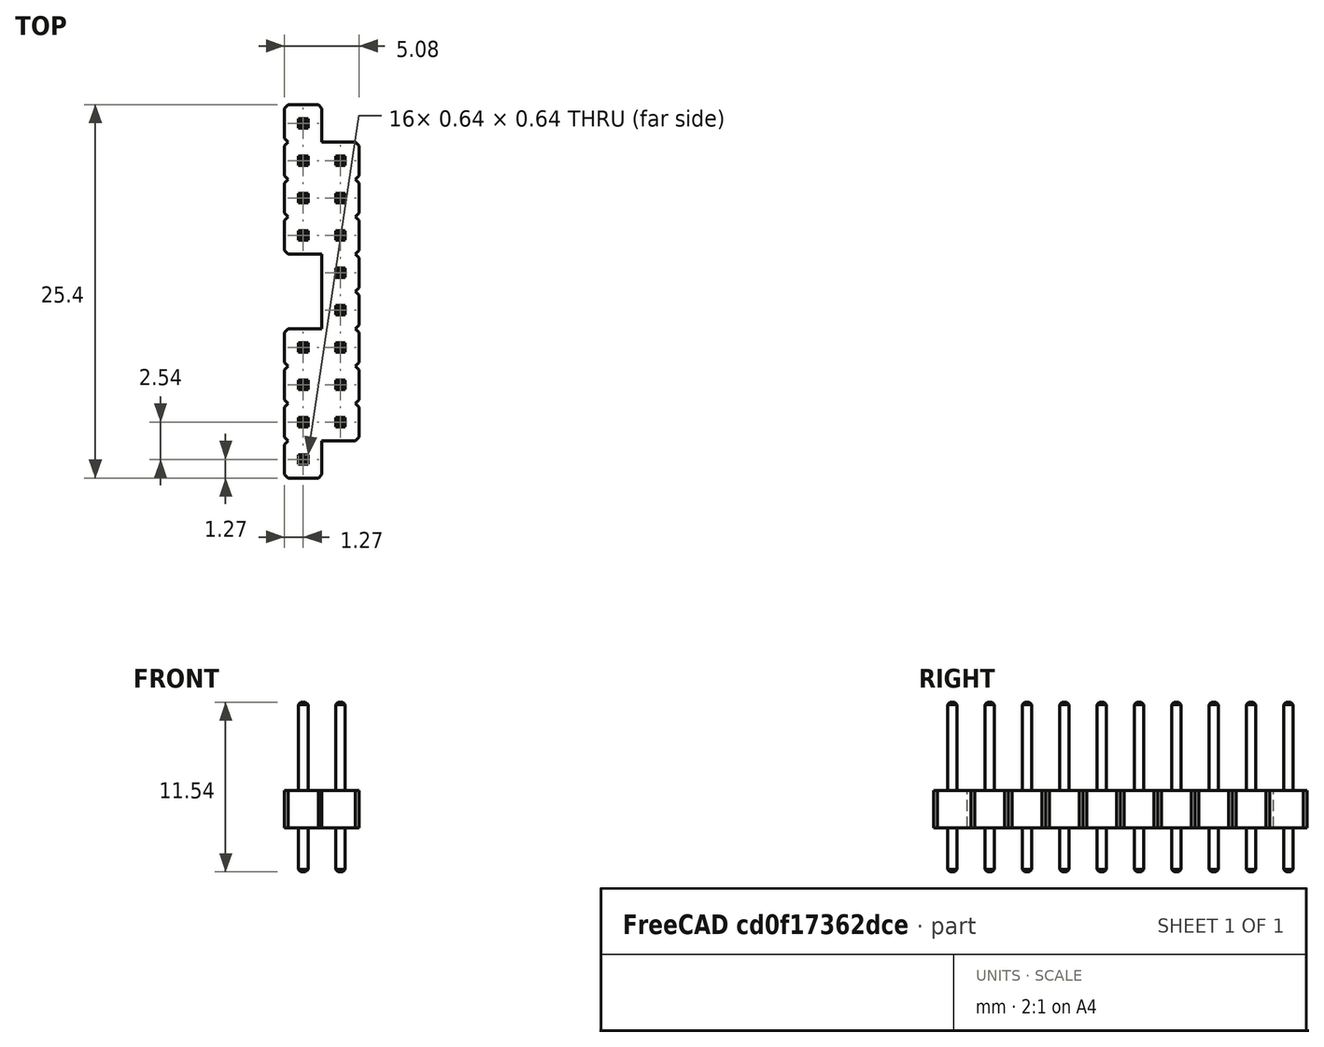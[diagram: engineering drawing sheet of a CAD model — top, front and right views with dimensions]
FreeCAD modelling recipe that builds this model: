
FCSTD DOCUMENT  (FreeCAD 0.18R16146 (Git))
Label: ce-header
License: All rights reserved
LicenseURL: http://en.wikipedia.org/wiki/All_rights_reserved
objects: Part::Box×3, Part::Cut×3, Part::Feature×1, Part::Chamfer×1
note: 8 computed .brp shape members not serialized (recipe doc carries the construction recipe); baked Part::Feature solids carry a one-line shape summary decoded from their .brp

FEATURE [Part::Feature] Part__Feature  label="PinHeader_2x10_P254mm_Vertical"
  shape: bbox 5.08 x 25.4 x 11.54 mm, 424 faces (baked)
FEATURE [Part::Box] Box  label="Cube"
  AttacherType = Attacher::AttachEngine3D
  Height = 20
  Length = 2.54
  Placement = pos=(1.27,-1.27,-8) rot=(0,0,1;0rad)
  Width = 2.54
FEATURE [Part::Cut] Cut
  Base = -> Part__Feature
  Tool = -> Box
FEATURE [Part::Box] Box001  label="Cube001"
  AttacherType = Attacher::AttachEngine3D
  Height = 20
  Length = 2.54
  Placement = pos=(1.27,-24.13,-8) rot=(0,0,1;0rad)
  Width = 2.54
FEATURE [Part::Box] Box002  label="Cube002"
  AttacherType = Attacher::AttachEngine3D
  Height = 20
  Length = 2.54
  Placement = pos=(-1.27,-13.97,-8) rot=(0,0,1;0rad)
  Width = 5.08
FEATURE [Part::Cut] Cut001
  Base = -> Cut
  Tool = -> Box001
FEATURE [Part::Cut] Cut002
  Base = -> Cut001
  Tool = -> Box002
FEATURE [Part::Chamfer] Chamfer
  Base = -> Cut002
  Edges = 2 edges r=0.25: [Edge7,Edge274]
